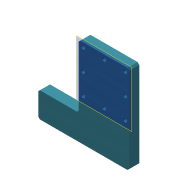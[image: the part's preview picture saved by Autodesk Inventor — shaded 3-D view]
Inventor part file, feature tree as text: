
AUTODESK INVENTOR PART (.ipt)
format: ipt  version: 2022 (Build 260153000, 153)  size: 198,144 bytes
history: native  units: mm
features: other x7, reference x5, sketch x3, hole x2, plane x1, extrude x1, chamfer x1, projected_geometry x1
ambient origin geometry x8: Origin, YZ Plane, XZ Plane, XY Plane, X Axis, Y Axis, Z Axis, Center Point
bodies: Body1 (feature_tree)
feature tree (21):
  plane  "Arbeitsebene2"
  extrude  "Extrusion1"  Depth=30.0mm
  chamfer  "Fase1"  Distance=45.0mm
  hole  "Bohrung2"  [1 undecoded]
  hole  "Bohrung3"  [1 undecoded]
  sketch  "Skizze6"  dims[d10=30.0mm d11=30.0mm]
  reference  "Referenz1"
  reference  "Referenz2"
  sketch  "Skizze7"  dims[d12=30.0mm]
  projected_geometry  "Projizierte Kontur2"
  sketch  "Skizze8"  dims[d13=30.0mm d14=45.0mm d15=18.0mm d16=12.0mm d17=0.0mm d18=2.0mm d19=2.0mm d20=45.0deg d21=5.0mm d22=6.0mm d23=8.0mm d24=5.0mm d25=90.0deg d26=8.0mm d27=20.594885mm d28=8.0mm d29=2.8mm d30=6.0mm d31=6.5mm d32=3.0mm d33=90.0deg d34=8.0mm d35=20.594885mm]
  reference  "Referenz3"
  reference  "Referenz4"
  reference  "Referenz5"
  other  "<userpath>\Documents\GitHub\cellstorm\INVENTOR\cellSTORM_v6.iam"
  other  "cellSTORM_v6.iam"
  other  "00_XY_stage-CHUO_SEIKI_LD-647-R1:1"
  other  "00_XY_stage-CHUO_SEIKI_LD-647-R1-Bottom:1"
  other  "cellSTORM_v5_microsocpe:1"
  other  "30_Cube_Z_Focus_MGN12_NEMA_slide_part2:1"
  other  "cellSTORM_v5_chiptray_old_0:1"
note: 2 required parameter values undecoded (feature->parameter linkage not recoverable at this tier; creation-order binding heuristic only, values carry confidence <= 0.55)
